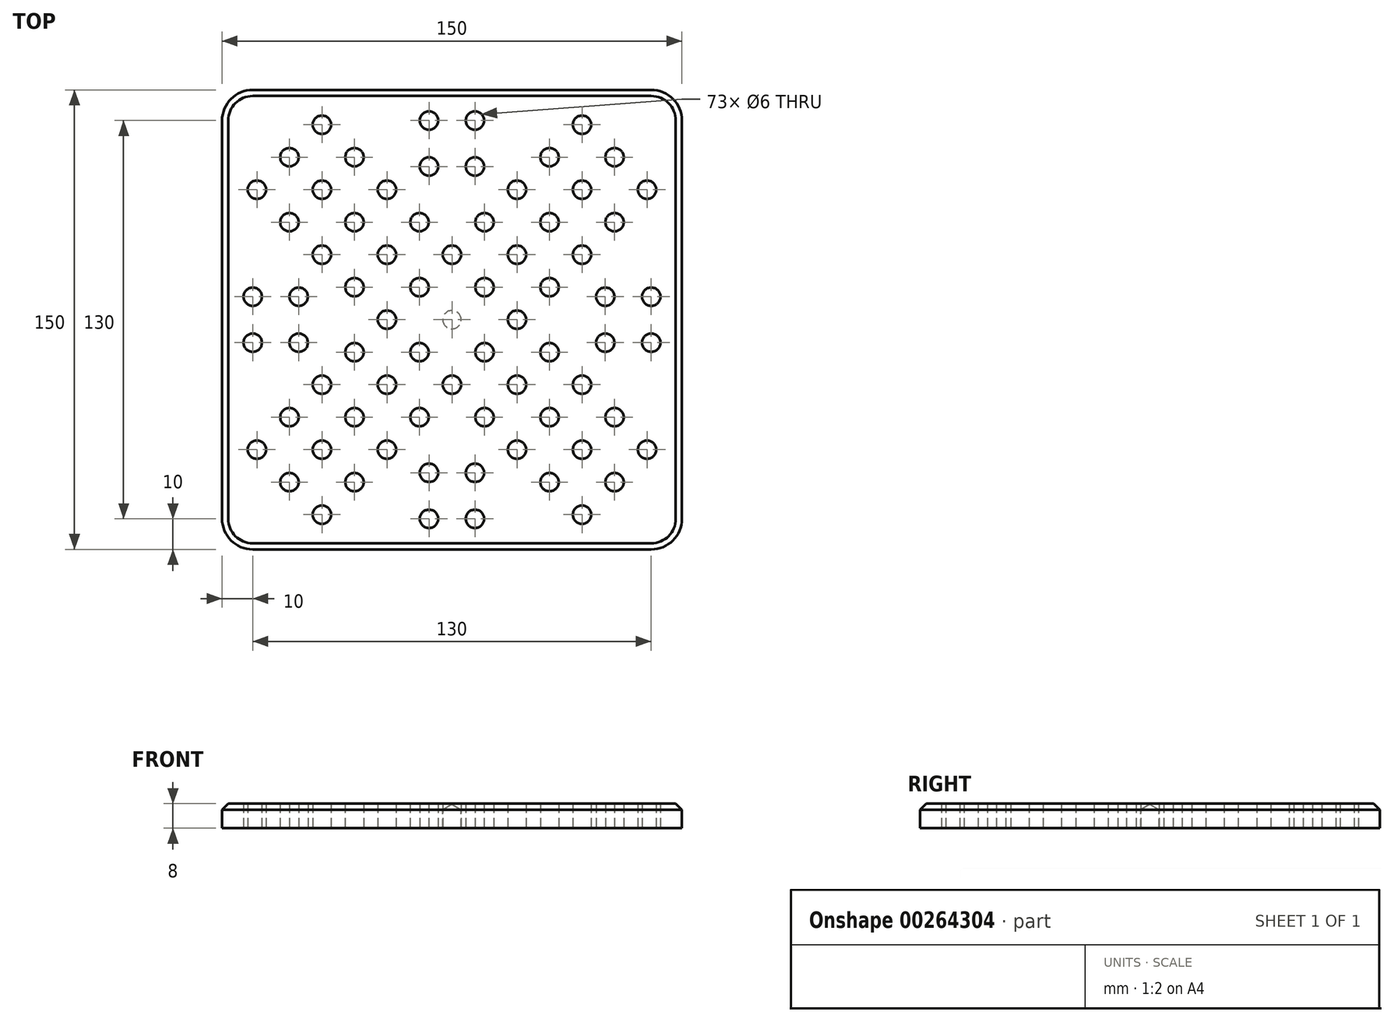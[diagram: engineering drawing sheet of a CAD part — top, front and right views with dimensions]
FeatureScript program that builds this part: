
annotation { "Feature Type Name" : "Feature", "Feature Type Description" : "" }
export const myFeature = defineFeature(function(context is Context, id is Id, definition is map)
    precondition{}
    {
        {
            var Q0;
            Q0=qCreatedBy(makeId("Top.planeOp"),FACE);
            var sketch = newSketch(context, id + "F0", { "sketchPlane" : qUnion([Q0])});
            skLineSegment(sketch, "E0.bottom", {"start": v(75, 75) * mm, "end": v(-75, 75) * mm});
            skLineSegment(sketch, "E0.top", {"start": v(75, -75) * mm, "end": v(-75, -75) * mm});
            skLineSegment(sketch, "E0.left", {"start": v(75, 75) * mm, "end": v(75, -75) * mm});
            skLineSegment(sketch, "E0.right", {"start": v(-75, 75) * mm, "end": v(-75, -75) * mm});
            skPoint(sketch, "E0.middle", {"position": v(0, 0) * mm});
            skLineSegment(sketch, "E1", {"start": v(-75, 75) * mm, "end": v(75, -75) * mm});
            skLineSegment(sketch, "E2", {"start": v(75, 75) * mm, "end": v(-75, -75) * mm});
            skCircle(sketch, "E3", {"center": v(-10.6, 10.6) * mm, "radius": 3 * mm});
            skCircle(sketch, "E4", {"center": v(-21.21, 0) * mm, "radius": 3 * mm});
            skCircle(sketch, "E5", {"center": v(-10.6, -10.6) * mm, "radius": 3 * mm});
            skCircle(sketch, "E6", {"center": v(-21.21, 21.21) * mm, "radius": 3 * mm});
            skCircle(sketch, "E7", {"center": v(-31.82, 31.82) * mm, "radius": 3 * mm});
            skCircle(sketch, "E8", {"center": v(-42.43, 42.43) * mm, "radius": 3 * mm});
            skCircle(sketch, "E9", {"center": v(-53.03, 53.03) * mm, "radius": 3 * mm});
            skCircle(sketch, "E10", {"center": v(-31.82, 10.6) * mm, "radius": 3 * mm});
            skCircle(sketch, "E11", {"center": v(-42.43, 21.21) * mm, "radius": 3 * mm});
            skCircle(sketch, "E12", {"center": v(-63.64, 42.43) * mm, "radius": 3 * mm});
            skCircle(sketch, "E13", {"center": v(-53.03, 31.82) * mm, "radius": 3 * mm});
            skCircle(sketch, "E14.MirrorC", {"center": v(0, 21.21) * mm, "radius": 3 * mm});
            skCircle(sketch, "E15.MirrorC", {"center": v(-42.43, 63.64) * mm, "radius": 3 * mm});
            skCircle(sketch, "E16.MirrorC", {"center": v(-21.21, 42.43) * mm, "radius": 3 * mm});
            skCircle(sketch, "E17.MirrorC", {"center": v(-10.6, 31.82) * mm, "radius": 3 * mm});
            skCircle(sketch, "E18.MirrorC", {"center": v(10.6, 10.6) * mm, "radius": 3 * mm});
            skCircle(sketch, "E19.MirrorC", {"center": v(-31.82, 53.03) * mm, "radius": 3 * mm});
            skCircle(sketch, "E20.MirrorC", {"center": v(21.21, 21.21) * mm, "radius": 3 * mm});
            skCircle(sketch, "E21.MirrorC", {"center": v(31.82, 31.82) * mm, "radius": 3 * mm});
            skCircle(sketch, "E22.MirrorC", {"center": v(42.43, 42.43) * mm, "radius": 3 * mm});
            skCircle(sketch, "E23.MirrorC", {"center": v(53.03, 53.03) * mm, "radius": 3 * mm});
            skCircle(sketch, "E24.MirrorC", {"center": v(21.21, 0) * mm, "radius": 3 * mm});
            skCircle(sketch, "E25.MirrorC", {"center": v(10.6, -10.6) * mm, "radius": 3 * mm});
            skCircle(sketch, "E26.MirrorC", {"center": v(42.43, 21.21) * mm, "radius": 3 * mm});
            skCircle(sketch, "E27.MirrorC", {"center": v(31.82, 53.03) * mm, "radius": 3 * mm});
            skCircle(sketch, "E28.MirrorC", {"center": v(63.64, 42.43) * mm, "radius": 3 * mm});
            skCircle(sketch, "E29.MirrorC", {"center": v(42.43, 63.64) * mm, "radius": 3 * mm});
            skCircle(sketch, "E30.MirrorC", {"center": v(31.82, 10.6) * mm, "radius": 3 * mm});
            skCircle(sketch, "E31.MirrorC", {"center": v(21.21, 42.43) * mm, "radius": 3 * mm});
            skCircle(sketch, "E32.MirrorC", {"center": v(53.03, 31.82) * mm, "radius": 3 * mm});
            skCircle(sketch, "E33.MirrorC", {"center": v(10.6, 31.82) * mm, "radius": 3 * mm});
            skCircle(sketch, "E34", {"center": v(-7.5, 50) * mm, "radius": 3 * mm});
            skCircle(sketch, "E35", {"center": v(7.5, 65) * mm, "radius": 3 * mm});
            skCircle(sketch, "E36", {"center": v(-7.5, 65) * mm, "radius": 3 * mm});
            skCircle(sketch, "E37", {"center": v(7.5, 50) * mm, "radius": 3 * mm});
            skCircle(sketch, "E38.MirrorC", {"center": v(50, 7.5) * mm, "radius": 3 * mm});
            skCircle(sketch, "E39.MirrorC", {"center": v(50, -7.5) * mm, "radius": 3 * mm});
            skCircle(sketch, "E40.MirrorC", {"center": v(65, 7.5) * mm, "radius": 3 * mm});
            skCircle(sketch, "E41.MirrorC", {"center": v(65, -7.5) * mm, "radius": 3 * mm});
            skCircle(sketch, "E42.MirrorC", {"center": v(7.5, -65) * mm, "radius": 3 * mm});
            skCircle(sketch, "E43.MirrorC", {"center": v(-7.5, -65) * mm, "radius": 3 * mm});
            skCircle(sketch, "E44.MirrorC", {"center": v(7.5, -50) * mm, "radius": 3 * mm});
            skCircle(sketch, "E45.MirrorC", {"center": v(-7.5, -50) * mm, "radius": 3 * mm});
            skCircle(sketch, "E46.MirrorC", {"center": v(-50, -7.5) * mm, "radius": 3 * mm});
            skCircle(sketch, "E47.MirrorC", {"center": v(-50, 7.5) * mm, "radius": 3 * mm});
            skCircle(sketch, "E48.MirrorC", {"center": v(-65, -7.5) * mm, "radius": 3 * mm});
            skCircle(sketch, "E49.MirrorC", {"center": v(-65, 7.5) * mm, "radius": 3 * mm});
            skCircle(sketch, "E50.MirrorC", {"center": v(42.43, -42.43) * mm, "radius": 3 * mm});
            skLineSegment(sketch, "E51.MirrorCS", {"start": v(-75, -75) * mm, "end": v(75, 75) * mm});
            skCircle(sketch, "E52.MirrorC", {"center": v(53.03, -53.03) * mm, "radius": 3 * mm});
            skCircle(sketch, "E53.MirrorC", {"center": v(-42.43, -42.43) * mm, "radius": 3 * mm});
            skCircle(sketch, "E54.MirrorC", {"center": v(-31.82, -31.82) * mm, "radius": 3 * mm});
            skCircle(sketch, "E55.MirrorC", {"center": v(31.82, -31.82) * mm, "radius": 3 * mm});
            skCircle(sketch, "E56.MirrorC", {"center": v(21.21, -21.21) * mm, "radius": 3 * mm});
            skCircle(sketch, "E57.MirrorC", {"center": v(-53.03, -53.03) * mm, "radius": 3 * mm});
            skCircle(sketch, "E58.MirrorC", {"center": v(0, -21.21) * mm, "radius": 3 * mm});
            skCircle(sketch, "E59.MirrorC", {"center": v(-21.21, -21.21) * mm, "radius": 3 * mm});
            skLineSegment(sketch, "E60.MirrorCS", {"start": v(75, -75) * mm, "end": v(-75, 75) * mm});
            skCircle(sketch, "E61.MirrorC", {"center": v(53.03, -31.82) * mm, "radius": 3 * mm});
            skCircle(sketch, "E62.MirrorC", {"center": v(10.6, -31.82) * mm, "radius": 3 * mm});
            skCircle(sketch, "E63.MirrorC", {"center": v(31.82, -53.03) * mm, "radius": 3 * mm});
            skCircle(sketch, "E64.MirrorC", {"center": v(31.82, -10.6) * mm, "radius": 3 * mm});
            skCircle(sketch, "E65.MirrorC", {"center": v(-42.43, -21.21) * mm, "radius": 3 * mm});
            skCircle(sketch, "E66.MirrorC", {"center": v(-53.03, -31.82) * mm, "radius": 3 * mm});
            skCircle(sketch, "E67.MirrorC", {"center": v(-63.64, -42.43) * mm, "radius": 3 * mm});
            skCircle(sketch, "E68.MirrorC", {"center": v(-42.43, -63.64) * mm, "radius": 3 * mm});
            skCircle(sketch, "E69.MirrorC", {"center": v(42.43, -63.64) * mm, "radius": 3 * mm});
            skCircle(sketch, "E70.MirrorC", {"center": v(-21.21, -42.43) * mm, "radius": 3 * mm});
            skCircle(sketch, "E71.MirrorC", {"center": v(21.21, -42.43) * mm, "radius": 3 * mm});
            skCircle(sketch, "E72.MirrorC", {"center": v(-10.6, -31.82) * mm, "radius": 3 * mm});
            skCircle(sketch, "E73.MirrorC", {"center": v(42.43, -21.21) * mm, "radius": 3 * mm});
            skCircle(sketch, "E74.MirrorC", {"center": v(-31.82, -10.6) * mm, "radius": 3 * mm});
            skCircle(sketch, "E75.MirrorC", {"center": v(-31.82, -53.03) * mm, "radius": 3 * mm});
            skCircle(sketch, "E76.MirrorC", {"center": v(63.64, -42.43) * mm, "radius": 3 * mm});
            skSolve(sketch);
        }
        {
            var Q0;
            Q0 = qSketchRegion(id + "F0", true);
            extrude(context, id + "F1", {"entities" : qUnion([Q0]), "depth" : 8 * mm});
        }
        {
            var Q0;
            Q0=makeQuery(id+"F1.opExtrude","SWEPT_EDGE",EDGE,{"disambiguationData":[OSD([sQuery(id+"F0.wireOp",EDGE,"E0.top"),sQuery(id+"F0.wireOp",EDGE,"E0.right"),sQuery(id+"F0.wireOp",EDGE,"E51.MirrorCS")])]});
            var Q1;
            Q1=makeQuery(id+"F1.opExtrude","SWEPT_EDGE",EDGE,{"disambiguationData":[OSD([sQuery(id+"F0.wireOp",EDGE,"E0.bottom"),sQuery(id+"F0.wireOp",EDGE,"E0.right"),sQuery(id+"F0.wireOp",EDGE,"E60.MirrorCS")])]});
            var Q2;
            Q2=makeQuery(id+"F1.opExtrude","SWEPT_EDGE",EDGE,{"disambiguationData":[OSD([sQuery(id+"F0.wireOp",EDGE,"E0.bottom"),sQuery(id+"F0.wireOp",EDGE,"E0.left"),sQuery(id+"F0.wireOp",EDGE,"E51.MirrorCS")])]});
            var Q3;
            Q3=makeQuery(id+"F1.opExtrude","SWEPT_EDGE",EDGE,{"disambiguationData":[OSD([sQuery(id+"F0.wireOp",EDGE,"E0.top"),sQuery(id+"F0.wireOp",EDGE,"E0.left"),sQuery(id+"F0.wireOp",EDGE,"E60.MirrorCS")])]});
            fillet(context, id + "F2", {"entities" : qUnion([Q0, Q1, Q2, Q3]), "radius" : 10 * mm, "tangentPropagation" : true, "allowEdgeOverflow" : false});
        }
        {
            var Q0;
            {var subQ0=sQuery(id+"F0.wireOp",EDGE,"E0.right");var subQ1=sQuery(id+"F0.wireOp",EDGE,"E0.top");Q0=makeQuery(id+"F2.opFillet","BLEND_EDGE",EDGE,{"blendedFrom":[makeQuery(id+"F1.opExtrude","SWEPT_EDGE",EDGE,{"disambiguationData":[OSD([subQ1,subQ0,sQuery(id+"F0.wireOp",EDGE,"E51.MirrorCS")])]}),makeQuery(id+"F1.opExtrude","CAP_FACE",FACE,{"disambiguationData":[OSD([sQuery(id+"F0.wireOp",EDGE,"E0.bottom"),subQ1,sQuery(id+"F0.wireOp",EDGE,"E0.left"),subQ0,sQuery(id+"F0.wireOp",EDGE,"E10"),sQuery(id+"F0.wireOp",EDGE,"E11"),sQuery(id+"F0.wireOp",EDGE,"E12"),sQuery(id+"F0.wireOp",EDGE,"E13"),sQuery(id+"F0.wireOp",EDGE,"E15.MirrorC"),sQuery(id+"F0.wireOp",EDGE,"E16.MirrorC"),sQuery(id+"F0.wireOp",EDGE,"E17.MirrorC"),sQuery(id+"F0.wireOp",EDGE,"E6"),sQuery(id+"F0.wireOp",EDGE,"E7"),sQuery(id+"F0.wireOp",EDGE,"E8"),sQuery(id+"F0.wireOp",EDGE,"E9"),sQuery(id+"F0.wireOp",EDGE,"E19.MirrorC"),sQuery(id+"F0.wireOp",EDGE,"E23.MirrorC"),sQuery(id+"F0.wireOp",EDGE,"E26.MirrorC"),sQuery(id+"F0.wireOp",EDGE,"E27.MirrorC"),sQuery(id+"F0.wireOp",EDGE,"E28.MirrorC"),sQuery(id+"F0.wireOp",EDGE,"E29.MirrorC"),sQuery(id+"F0.wireOp",EDGE,"E20.MirrorC"),sQuery(id+"F0.wireOp",EDGE,"E30.MirrorC"),sQuery(id+"F0.wireOp",EDGE,"E31.MirrorC"),sQuery(id+"F0.wireOp",EDGE,"E32.MirrorC"),sQuery(id+"F0.wireOp",EDGE,"E21.MirrorC"),sQuery(id+"F0.wireOp",EDGE,"E33.MirrorC"),sQuery(id+"F0.wireOp",EDGE,"E22.MirrorC"),sQuery(id+"F0.wireOp",EDGE,"E14.MirrorC"),sQuery(id+"F0.wireOp",EDGE,"E34"),sQuery(id+"F0.wireOp",EDGE,"E35"),sQuery(id+"F0.wireOp",EDGE,"E36"),sQuery(id+"F0.wireOp",EDGE,"E37"),sQuery(id+"F0.wireOp",EDGE,"E44.MirrorC"),sQuery(id+"F0.wireOp",EDGE,"E43.MirrorC"),sQuery(id+"F0.wireOp",EDGE,"E61.MirrorC"),sQuery(id+"F0.wireOp",EDGE,"E57.MirrorC"),sQuery(id+"F0.wireOp",EDGE,"E56.MirrorC"),sQuery(id+"F0.wireOp",EDGE,"E45.MirrorC"),sQuery(id+"F0.wireOp",EDGE,"E62.MirrorC"),sQuery(id+"F0.wireOp",EDGE,"E63.MirrorC"),sQuery(id+"F0.wireOp",EDGE,"E64.MirrorC"),sQuery(id+"F0.wireOp",EDGE,"E59.MirrorC"),sQuery(id+"F0.wireOp",EDGE,"E65.MirrorC"),sQuery(id+"F0.wireOp",EDGE,"E42.MirrorC"),sQuery(id+"F0.wireOp",EDGE,"E52.MirrorC"),sQuery(id+"F0.wireOp",EDGE,"E25.MirrorC"),sQuery(id+"F0.wireOp",EDGE,"E47.MirrorC"),sQuery(id+"F0.wireOp",EDGE,"E4"),sQuery(id+"F0.wireOp",EDGE,"E66.MirrorC"),sQuery(id+"F0.wireOp",EDGE,"E18.MirrorC"),sQuery(id+"F0.wireOp",EDGE,"E5"),sQuery(id+"F0.wireOp",EDGE,"E67.MirrorC"),sQuery(id+"F0.wireOp",EDGE,"E49.MirrorC"),sQuery(id+"F0.wireOp",EDGE,"E58.MirrorC"),sQuery(id+"F0.wireOp",EDGE,"E41.MirrorC"),sQuery(id+"F0.wireOp",EDGE,"E68.MirrorC"),sQuery(id+"F0.wireOp",EDGE,"E53.MirrorC"),sQuery(id+"F0.wireOp",EDGE,"E69.MirrorC"),sQuery(id+"F0.wireOp",EDGE,"E38.MirrorC"),sQuery(id+"F0.wireOp",EDGE,"E24.MirrorC"),sQuery(id+"F0.wireOp",EDGE,"E48.MirrorC"),sQuery(id+"F0.wireOp",EDGE,"E50.MirrorC"),sQuery(id+"F0.wireOp",EDGE,"E46.MirrorC"),sQuery(id+"F0.wireOp",EDGE,"E3"),sQuery(id+"F0.wireOp",EDGE,"E70.MirrorC"),sQuery(id+"F0.wireOp",EDGE,"E71.MirrorC"),sQuery(id+"F0.wireOp",EDGE,"E72.MirrorC"),sQuery(id+"F0.wireOp",EDGE,"E73.MirrorC"),sQuery(id+"F0.wireOp",EDGE,"E74.MirrorC"),sQuery(id+"F0.wireOp",EDGE,"E75.MirrorC"),sQuery(id+"F0.wireOp",EDGE,"E40.MirrorC"),sQuery(id+"F0.wireOp",EDGE,"E55.MirrorC"),sQuery(id+"F0.wireOp",EDGE,"E39.MirrorC"),sQuery(id+"F0.wireOp",EDGE,"E76.MirrorC"),sQuery(id+"F0.wireOp",EDGE,"E54.MirrorC"),sQuery(id+"F0.wireOp",EDGE,"FkDd4gIT-RVA1-L8L9-rlqA-te1O1rxEWN5e")])],"isStart":false})],"blendedInto":[makeQuery(id+"F1.opExtrude","CAP_FACE",FACE,{"disambiguationData":[OSD([sQuery(id+"F0.wireOp",EDGE,"E0.bottom"),subQ1,sQuery(id+"F0.wireOp",EDGE,"E0.left"),subQ0,sQuery(id+"F0.wireOp",EDGE,"E10"),sQuery(id+"F0.wireOp",EDGE,"E11"),sQuery(id+"F0.wireOp",EDGE,"E12"),sQuery(id+"F0.wireOp",EDGE,"E13"),sQuery(id+"F0.wireOp",EDGE,"E15.MirrorC"),sQuery(id+"F0.wireOp",EDGE,"E16.MirrorC"),sQuery(id+"F0.wireOp",EDGE,"E17.MirrorC"),sQuery(id+"F0.wireOp",EDGE,"E6"),sQuery(id+"F0.wireOp",EDGE,"E7"),sQuery(id+"F0.wireOp",EDGE,"E8"),sQuery(id+"F0.wireOp",EDGE,"E9"),sQuery(id+"F0.wireOp",EDGE,"E19.MirrorC"),sQuery(id+"F0.wireOp",EDGE,"E23.MirrorC"),sQuery(id+"F0.wireOp",EDGE,"E26.MirrorC"),sQuery(id+"F0.wireOp",EDGE,"E27.MirrorC"),sQuery(id+"F0.wireOp",EDGE,"E28.MirrorC"),sQuery(id+"F0.wireOp",EDGE,"E29.MirrorC"),sQuery(id+"F0.wireOp",EDGE,"E20.MirrorC"),sQuery(id+"F0.wireOp",EDGE,"E30.MirrorC"),sQuery(id+"F0.wireOp",EDGE,"E31.MirrorC"),sQuery(id+"F0.wireOp",EDGE,"E32.MirrorC"),sQuery(id+"F0.wireOp",EDGE,"E21.MirrorC"),sQuery(id+"F0.wireOp",EDGE,"E33.MirrorC"),sQuery(id+"F0.wireOp",EDGE,"E22.MirrorC"),sQuery(id+"F0.wireOp",EDGE,"E14.MirrorC"),sQuery(id+"F0.wireOp",EDGE,"E34"),sQuery(id+"F0.wireOp",EDGE,"E35"),sQuery(id+"F0.wireOp",EDGE,"E36"),sQuery(id+"F0.wireOp",EDGE,"E37"),sQuery(id+"F0.wireOp",EDGE,"E44.MirrorC"),sQuery(id+"F0.wireOp",EDGE,"E43.MirrorC"),sQuery(id+"F0.wireOp",EDGE,"E61.MirrorC"),sQuery(id+"F0.wireOp",EDGE,"E57.MirrorC"),sQuery(id+"F0.wireOp",EDGE,"E56.MirrorC"),sQuery(id+"F0.wireOp",EDGE,"E45.MirrorC"),sQuery(id+"F0.wireOp",EDGE,"E62.MirrorC"),sQuery(id+"F0.wireOp",EDGE,"E63.MirrorC"),sQuery(id+"F0.wireOp",EDGE,"E64.MirrorC"),sQuery(id+"F0.wireOp",EDGE,"E59.MirrorC"),sQuery(id+"F0.wireOp",EDGE,"E65.MirrorC"),sQuery(id+"F0.wireOp",EDGE,"E42.MirrorC"),sQuery(id+"F0.wireOp",EDGE,"E52.MirrorC"),sQuery(id+"F0.wireOp",EDGE,"E25.MirrorC"),sQuery(id+"F0.wireOp",EDGE,"E47.MirrorC"),sQuery(id+"F0.wireOp",EDGE,"E4"),sQuery(id+"F0.wireOp",EDGE,"E66.MirrorC"),sQuery(id+"F0.wireOp",EDGE,"E18.MirrorC"),sQuery(id+"F0.wireOp",EDGE,"E5"),sQuery(id+"F0.wireOp",EDGE,"E67.MirrorC"),sQuery(id+"F0.wireOp",EDGE,"E49.MirrorC"),sQuery(id+"F0.wireOp",EDGE,"E58.MirrorC"),sQuery(id+"F0.wireOp",EDGE,"E41.MirrorC"),sQuery(id+"F0.wireOp",EDGE,"E68.MirrorC"),sQuery(id+"F0.wireOp",EDGE,"E53.MirrorC"),sQuery(id+"F0.wireOp",EDGE,"E69.MirrorC"),sQuery(id+"F0.wireOp",EDGE,"E38.MirrorC"),sQuery(id+"F0.wireOp",EDGE,"E24.MirrorC"),sQuery(id+"F0.wireOp",EDGE,"E48.MirrorC"),sQuery(id+"F0.wireOp",EDGE,"E50.MirrorC"),sQuery(id+"F0.wireOp",EDGE,"E46.MirrorC"),sQuery(id+"F0.wireOp",EDGE,"E3"),sQuery(id+"F0.wireOp",EDGE,"E70.MirrorC"),sQuery(id+"F0.wireOp",EDGE,"E71.MirrorC"),sQuery(id+"F0.wireOp",EDGE,"E72.MirrorC"),sQuery(id+"F0.wireOp",EDGE,"E73.MirrorC"),sQuery(id+"F0.wireOp",EDGE,"E74.MirrorC"),sQuery(id+"F0.wireOp",EDGE,"E75.MirrorC"),sQuery(id+"F0.wireOp",EDGE,"E40.MirrorC"),sQuery(id+"F0.wireOp",EDGE,"E55.MirrorC"),sQuery(id+"F0.wireOp",EDGE,"E39.MirrorC"),sQuery(id+"F0.wireOp",EDGE,"E76.MirrorC"),sQuery(id+"F0.wireOp",EDGE,"E54.MirrorC"),sQuery(id+"F0.wireOp",EDGE,"FkDd4gIT-RVA1-L8L9-rlqA-te1O1rxEWN5e")])],"isStart":false})]});}
            chamfer(context, id + "F3", {"entities" : qUnion([Q0]), "width" : 2 * mm, "tangentPropagation" : true});
        }
        {
            var Q0;
            Q0=sQuery(id+"F0.wireOp",VERTEX,"E0.middle");
            var Q1;
            Q1=makeQuery(id+"F1.opExtrude","SWEPT_BODY",BODY,{"disambiguationData":[OSD([sQuery(id+"F0.wireOp",EDGE,"E0.bottom"),sQuery(id+"F0.wireOp",EDGE,"E0.top"),sQuery(id+"F0.wireOp",EDGE,"E0.left"),sQuery(id+"F0.wireOp",EDGE,"E0.right"),sQuery(id+"F0.wireOp",EDGE,"E10"),sQuery(id+"F0.wireOp",EDGE,"E11"),sQuery(id+"F0.wireOp",EDGE,"E12"),sQuery(id+"F0.wireOp",EDGE,"E13"),sQuery(id+"F0.wireOp",EDGE,"E15.MirrorC"),sQuery(id+"F0.wireOp",EDGE,"E16.MirrorC"),sQuery(id+"F0.wireOp",EDGE,"E17.MirrorC"),sQuery(id+"F0.wireOp",EDGE,"E6"),sQuery(id+"F0.wireOp",EDGE,"E7"),sQuery(id+"F0.wireOp",EDGE,"E8"),sQuery(id+"F0.wireOp",EDGE,"E9"),sQuery(id+"F0.wireOp",EDGE,"E19.MirrorC"),sQuery(id+"F0.wireOp",EDGE,"E23.MirrorC"),sQuery(id+"F0.wireOp",EDGE,"E26.MirrorC"),sQuery(id+"F0.wireOp",EDGE,"E27.MirrorC"),sQuery(id+"F0.wireOp",EDGE,"E28.MirrorC"),sQuery(id+"F0.wireOp",EDGE,"E29.MirrorC"),sQuery(id+"F0.wireOp",EDGE,"E20.MirrorC"),sQuery(id+"F0.wireOp",EDGE,"E30.MirrorC"),sQuery(id+"F0.wireOp",EDGE,"E31.MirrorC"),sQuery(id+"F0.wireOp",EDGE,"E32.MirrorC"),sQuery(id+"F0.wireOp",EDGE,"E21.MirrorC"),sQuery(id+"F0.wireOp",EDGE,"E33.MirrorC"),sQuery(id+"F0.wireOp",EDGE,"E22.MirrorC"),sQuery(id+"F0.wireOp",EDGE,"E14.MirrorC"),sQuery(id+"F0.wireOp",EDGE,"E34"),sQuery(id+"F0.wireOp",EDGE,"E35"),sQuery(id+"F0.wireOp",EDGE,"E36"),sQuery(id+"F0.wireOp",EDGE,"E37"),sQuery(id+"F0.wireOp",EDGE,"E44.MirrorC"),sQuery(id+"F0.wireOp",EDGE,"E43.MirrorC"),sQuery(id+"F0.wireOp",EDGE,"E61.MirrorC"),sQuery(id+"F0.wireOp",EDGE,"E57.MirrorC"),sQuery(id+"F0.wireOp",EDGE,"E56.MirrorC"),sQuery(id+"F0.wireOp",EDGE,"E45.MirrorC"),sQuery(id+"F0.wireOp",EDGE,"E62.MirrorC"),sQuery(id+"F0.wireOp",EDGE,"E63.MirrorC"),sQuery(id+"F0.wireOp",EDGE,"E64.MirrorC"),sQuery(id+"F0.wireOp",EDGE,"E59.MirrorC"),sQuery(id+"F0.wireOp",EDGE,"E65.MirrorC"),sQuery(id+"F0.wireOp",EDGE,"E42.MirrorC"),sQuery(id+"F0.wireOp",EDGE,"E52.MirrorC"),sQuery(id+"F0.wireOp",EDGE,"E25.MirrorC"),sQuery(id+"F0.wireOp",EDGE,"E47.MirrorC"),sQuery(id+"F0.wireOp",EDGE,"E4"),sQuery(id+"F0.wireOp",EDGE,"E66.MirrorC"),sQuery(id+"F0.wireOp",EDGE,"E18.MirrorC"),sQuery(id+"F0.wireOp",EDGE,"E5"),sQuery(id+"F0.wireOp",EDGE,"E67.MirrorC"),sQuery(id+"F0.wireOp",EDGE,"E49.MirrorC"),sQuery(id+"F0.wireOp",EDGE,"E58.MirrorC"),sQuery(id+"F0.wireOp",EDGE,"E41.MirrorC"),sQuery(id+"F0.wireOp",EDGE,"E68.MirrorC"),sQuery(id+"F0.wireOp",EDGE,"E53.MirrorC"),sQuery(id+"F0.wireOp",EDGE,"E69.MirrorC"),sQuery(id+"F0.wireOp",EDGE,"E38.MirrorC"),sQuery(id+"F0.wireOp",EDGE,"E24.MirrorC"),sQuery(id+"F0.wireOp",EDGE,"E48.MirrorC"),sQuery(id+"F0.wireOp",EDGE,"E50.MirrorC"),sQuery(id+"F0.wireOp",EDGE,"E46.MirrorC"),sQuery(id+"F0.wireOp",EDGE,"E3"),sQuery(id+"F0.wireOp",EDGE,"E70.MirrorC"),sQuery(id+"F0.wireOp",EDGE,"E71.MirrorC"),sQuery(id+"F0.wireOp",EDGE,"E72.MirrorC"),sQuery(id+"F0.wireOp",EDGE,"E73.MirrorC"),sQuery(id+"F0.wireOp",EDGE,"E74.MirrorC"),sQuery(id+"F0.wireOp",EDGE,"E75.MirrorC"),sQuery(id+"F0.wireOp",EDGE,"E40.MirrorC"),sQuery(id+"F0.wireOp",EDGE,"E55.MirrorC"),sQuery(id+"F0.wireOp",EDGE,"E39.MirrorC"),sQuery(id+"F0.wireOp",EDGE,"E76.MirrorC"),sQuery(id+"F0.wireOp",EDGE,"E54.MirrorC")])]});
            hole(context, id + "F4", {"style" : HoleStyle.SIMPLE, "endStyle" : HoleEndStyle.BLIND, "oppositeDirection" : true, "holeDiameter" : 6 * mm, "holeDepth" : 6 * mm, "tappedDepth" : 12 * mm, "tapClearance" : 3, "startFromSketch" : true, "locations" : qUnion([Q0]), "scope" : qUnion([Q1])});
        }
    });
